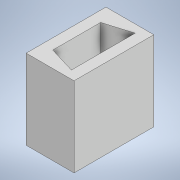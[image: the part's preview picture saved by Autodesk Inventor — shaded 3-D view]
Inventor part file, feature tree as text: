
AUTODESK INVENTOR PART (.ipt)
format: ipt  version: 2021 (Build 250183000, 183)  size: 110,592 bytes
history: native  units: in
note: dims shown in document units (in); Inventor stores cm internally (conversion verified against a paired STEP export)
features: extrude x2, sketch x2, chamfer x1
ambient origin geometry x8: Origin, YZ Plane, XZ Plane, XY Plane, X Axis, Y Axis, Z Axis, Center Point
bodies: Solid1 (feature_tree)
feature tree (5):
  extrude  "Extrusion1"  Depth=0.5906in
  extrude  "Extrusion2"  Depth=0.0787in
  chamfer  "Chamfer1"  Distance=0.0984in
  sketch  "Sketch1"  dims[d0=0.5906in d1=0.5906in]
  sketch  "Sketch2"  dims[d2=0.5906in d3=0.0in d5=0.0984in d6=0.0984in d7=0.5118in d8=0.0in d9=0.0591in d10=0.0591in d11=0.1181in d12=0.1181in d13=0.1969in d14=0.0787in d15=15.0deg]
